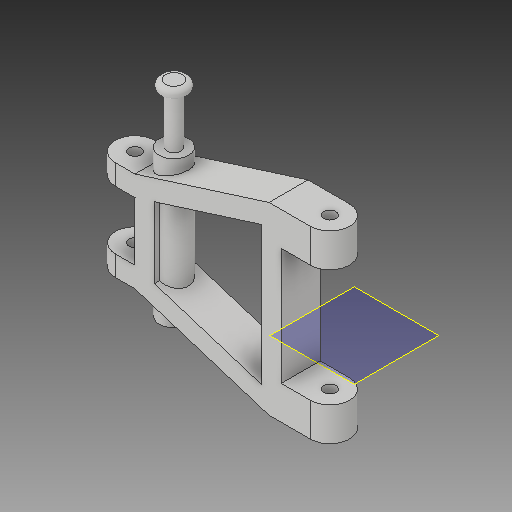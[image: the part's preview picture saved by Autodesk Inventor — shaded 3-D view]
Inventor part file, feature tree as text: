
AUTODESK INVENTOR PART (.ipt)
format: ipt  version: 2019 (Build 230136000, 136)  size: 182,784 bytes
history: native  units: in
note: dims shown in document units (in); Inventor stores cm internally (conversion verified against a paired STEP export)
features: sketch x4, other x3, plane x1
ambient origin geometry x8: Origin, YZ Plane, XZ Plane, XY Plane, X Axis, Y Axis, Z Axis, Center Point
bodies: Solid1 (feature_tree)
feature tree (8):
  other  "A_Arm.ipt"
  other  "Solid1::A_Arm.ipt"
  other  "TaggingFeature1"
  sketch  "Sketch2"  dims[d0=0.3937in]
  sketch  "Sketch3"
  sketch  "Sketch4"
  sketch  "Sketch5"
  plane  "Work Plane1"
